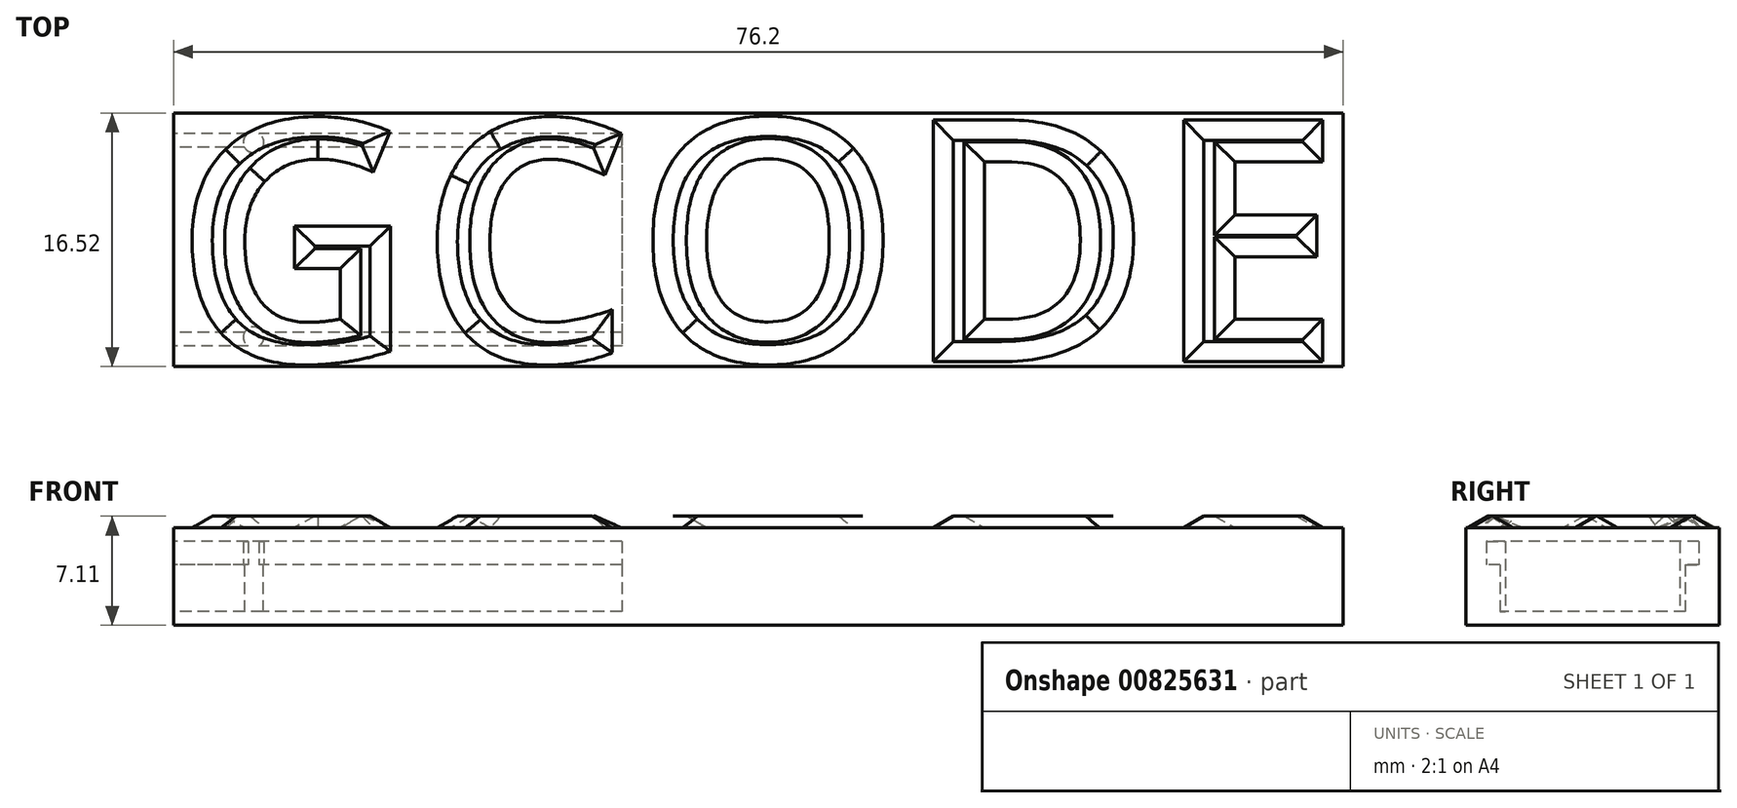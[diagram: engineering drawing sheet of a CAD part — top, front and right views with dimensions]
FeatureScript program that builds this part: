
annotation { "Feature Type Name" : "Feature", "Feature Type Description" : "" }
export const myFeature = defineFeature(function(context is Context, id is Id, definition is map)
    precondition{}
    {
        {
            var Q0;
            Q0=qCreatedBy(makeId("Top.planeOp"),FACE);
            var sketch = newSketch(context, id + "F0", { "sketchPlane" : qUnion([Q0])});
            skText(sketch, "E0", { "text": "GCODE", "fontName": "OpenSans-Bold.ttf"});
            const initialGuessF0  = {"E0": [-0.03818, -0.00794, 1, 0, 0.01588]};
            skSetInitialGuess(sketch, initialGuessF0);
            skSolve(sketch);
        }
        {
            var Q0;
            Q0=makeQuery(id+"F0.imprint","IMPRINT",FACE,{"disambiguationData":[TD([[makeQuery(id+"F0.imprint","IMPRINT",EDGE,{"derivedFrom":sQuery(id+"F0.wireOp",EDGE,"E0.sketch_text.stroke-0")}),-1.0]])]});
            var Q1;
            Q1=makeQuery(id+"F0.imprint","IMPRINT",FACE,{"disambiguationData":[TD([[makeQuery(id+"F0.imprint","IMPRINT",EDGE,{"derivedFrom":sQuery(id+"F0.wireOp",EDGE,"E0.sketch_text.stroke-19")}),-1.0]])]});
            var Q2;
            Q2=makeQuery(id+"F0.imprint","IMPRINT",FACE,{"disambiguationData":[TD([[makeQuery(id+"F0.imprint","IMPRINT",EDGE,{"derivedFrom":sQuery(id+"F0.wireOp",EDGE,"E0.sketch_text.stroke-48")}),-1.0]])]});
            var Q3;
            Q3=makeQuery(id+"F0.imprint","IMPRINT",FACE,{"disambiguationData":[TD([[makeQuery(id+"F0.imprint","IMPRINT",EDGE,{"derivedFrom":sQuery(id+"F0.wireOp",EDGE,"E0.sketch_text.stroke-34")}),-1.0]])]});
            var Q4;
            Q4=makeQuery(id+"F0.imprint","IMPRINT",FACE,{"disambiguationData":[TD([[makeQuery(id+"F0.imprint","IMPRINT",EDGE,{"derivedFrom":sQuery(id+"F0.wireOp",EDGE,"E0.sketch_text.stroke-60")}),-1.0]])]});
            extrude(context, id + "F1", {"entities" : qUnion([Q0, Q1, Q2, Q3, Q4]), "depth" : 0.76 * mm, "offsetDistance" : 25.4 * mm});
        }
        {
            var Q0;
            Q0=qCreatedBy(makeId("Right.planeOp"),FACE);
            var sketch = newSketch(context, id + "F2", { "sketchPlane" : qUnion([Q0])});
            skLineSegment(sketch, "E1.bottom", {"start": v(8.26, 0) * mm, "end": v(-8.26, 0) * mm});
            skLineSegment(sketch, "E1.top", {"start": v(8.26, -6.35) * mm, "end": v(-8.25, -6.35) * mm});
            skLineSegment(sketch, "E1.left", {"start": v(8.26, 0) * mm, "end": v(8.26, -6.35) * mm});
            skLineSegment(sketch, "E1.right", {"start": v(-8.26, 0) * mm, "end": v(-8.25, -6.35) * mm});
            skSolve(sketch);
        }
        {
            var Q0;
            Q0=makeQuery(id+"F2.imprint","IMPRINT",FACE,{"disambiguationData":[TD([[makeQuery(id+"F2.imprint","IMPRINT",EDGE,{"derivedFrom":sQuery(id+"F2.wireOp",EDGE,"E1.bottom")}),1.0]])]});
            extrude(context, id + "F3", {"entities" : qUnion([Q0]), "operationType" : NewBodyOperationType.ADD, "endBound" : BoundingType.SYMMETRIC, "depth" : 76.2 * mm, "offsetDistance" : 25.4 * mm});
        }
        {
            var Q0;
            Q0=makeQuery(id+"F1.opExtrude","CAP_EDGE",EDGE,{"disambiguationData":[OSD([sQuery(id+"F0.wireOp",EDGE,"E0.sketch_text.stroke-57")])],"isStart":false});
            var Q1;
            Q1=makeQuery(id+"F1.opExtrude","CAP_FACE",FACE,{"disambiguationData":[OSD([sQuery(id+"F0.wireOp",EDGE,"E0.sketch_text.stroke-48"),sQuery(id+"F0.wireOp",EDGE,"E0.sketch_text.stroke-49"),sQuery(id+"F0.wireOp",EDGE,"E0.sketch_text.stroke-50"),sQuery(id+"F0.wireOp",EDGE,"E0.sketch_text.stroke-51"),sQuery(id+"F0.wireOp",EDGE,"E0.sketch_text.stroke-52"),sQuery(id+"F0.wireOp",EDGE,"E0.sketch_text.stroke-53"),sQuery(id+"F0.wireOp",EDGE,"E0.sketch_text.stroke-54"),sQuery(id+"F0.wireOp",EDGE,"E0.sketch_text.stroke-55"),sQuery(id+"F0.wireOp",EDGE,"E0.sketch_text.stroke-56"),sQuery(id+"F0.wireOp",EDGE,"E0.sketch_text.stroke-57"),sQuery(id+"F0.wireOp",EDGE,"E0.sketch_text.stroke-58"),sQuery(id+"F0.wireOp",EDGE,"E0.sketch_text.stroke-59")])],"isStart":false});
            var Q2;
            Q2=makeQuery(id+"F1.opExtrude","CAP_FACE",FACE,{"disambiguationData":[OSD([sQuery(id+"F0.wireOp",EDGE,"E0.sketch_text.stroke-34"),sQuery(id+"F0.wireOp",EDGE,"E0.sketch_text.stroke-35"),sQuery(id+"F0.wireOp",EDGE,"E0.sketch_text.stroke-36"),sQuery(id+"F0.wireOp",EDGE,"E0.sketch_text.stroke-37"),sQuery(id+"F0.wireOp",EDGE,"E0.sketch_text.stroke-38"),sQuery(id+"F0.wireOp",EDGE,"E0.sketch_text.stroke-39"),sQuery(id+"F0.wireOp",EDGE,"E0.sketch_text.stroke-40"),sQuery(id+"F0.wireOp",EDGE,"E0.sketch_text.stroke-41"),sQuery(id+"F0.wireOp",EDGE,"E0.sketch_text.stroke-42"),sQuery(id+"F0.wireOp",EDGE,"E0.sketch_text.stroke-43"),sQuery(id+"F0.wireOp",EDGE,"E0.sketch_text.stroke-44"),sQuery(id+"F0.wireOp",EDGE,"E0.sketch_text.stroke-45"),sQuery(id+"F0.wireOp",EDGE,"E0.sketch_text.stroke-46"),sQuery(id+"F0.wireOp",EDGE,"E0.sketch_text.stroke-47")])],"isStart":false});
            var Q3;
            Q3=makeQuery(id+"F1.opExtrude","CAP_FACE",FACE,{"disambiguationData":[OSD([sQuery(id+"F0.wireOp",EDGE,"E0.sketch_text.stroke-60"),sQuery(id+"F0.wireOp",EDGE,"E0.sketch_text.stroke-61"),sQuery(id+"F0.wireOp",EDGE,"E0.sketch_text.stroke-62"),sQuery(id+"F0.wireOp",EDGE,"E0.sketch_text.stroke-63"),sQuery(id+"F0.wireOp",EDGE,"E0.sketch_text.stroke-64"),sQuery(id+"F0.wireOp",EDGE,"E0.sketch_text.stroke-65"),sQuery(id+"F0.wireOp",EDGE,"E0.sketch_text.stroke-66"),sQuery(id+"F0.wireOp",EDGE,"E0.sketch_text.stroke-67"),sQuery(id+"F0.wireOp",EDGE,"E0.sketch_text.stroke-68"),sQuery(id+"F0.wireOp",EDGE,"E0.sketch_text.stroke-69"),sQuery(id+"F0.wireOp",EDGE,"E0.sketch_text.stroke-70"),sQuery(id+"F0.wireOp",EDGE,"E0.sketch_text.stroke-71")])],"isStart":false});
            var Q4;
            Q4=makeQuery(id+"F1.opExtrude","CAP_FACE",FACE,{"disambiguationData":[OSD([sQuery(id+"F0.wireOp",EDGE,"E0.sketch_text.stroke-19"),sQuery(id+"F0.wireOp",EDGE,"E0.sketch_text.stroke-20"),sQuery(id+"F0.wireOp",EDGE,"E0.sketch_text.stroke-21"),sQuery(id+"F0.wireOp",EDGE,"E0.sketch_text.stroke-22"),sQuery(id+"F0.wireOp",EDGE,"E0.sketch_text.stroke-23"),sQuery(id+"F0.wireOp",EDGE,"E0.sketch_text.stroke-24"),sQuery(id+"F0.wireOp",EDGE,"E0.sketch_text.stroke-25"),sQuery(id+"F0.wireOp",EDGE,"E0.sketch_text.stroke-26"),sQuery(id+"F0.wireOp",EDGE,"E0.sketch_text.stroke-27"),sQuery(id+"F0.wireOp",EDGE,"E0.sketch_text.stroke-28"),sQuery(id+"F0.wireOp",EDGE,"E0.sketch_text.stroke-29"),sQuery(id+"F0.wireOp",EDGE,"E0.sketch_text.stroke-30"),sQuery(id+"F0.wireOp",EDGE,"E0.sketch_text.stroke-31"),sQuery(id+"F0.wireOp",EDGE,"E0.sketch_text.stroke-32"),sQuery(id+"F0.wireOp",EDGE,"E0.sketch_text.stroke-33")])],"isStart":false});
            var Q5;
            Q5=makeQuery(id+"F1.opExtrude","CAP_FACE",FACE,{"disambiguationData":[OSD([sQuery(id+"F0.wireOp",EDGE,"E0.sketch_text.stroke-0"),sQuery(id+"F0.wireOp",EDGE,"E0.sketch_text.stroke-1"),sQuery(id+"F0.wireOp",EDGE,"E0.sketch_text.stroke-2"),sQuery(id+"F0.wireOp",EDGE,"E0.sketch_text.stroke-3"),sQuery(id+"F0.wireOp",EDGE,"E0.sketch_text.stroke-4"),sQuery(id+"F0.wireOp",EDGE,"E0.sketch_text.stroke-5"),sQuery(id+"F0.wireOp",EDGE,"E0.sketch_text.stroke-6"),sQuery(id+"F0.wireOp",EDGE,"E0.sketch_text.stroke-7"),sQuery(id+"F0.wireOp",EDGE,"E0.sketch_text.stroke-8"),sQuery(id+"F0.wireOp",EDGE,"E0.sketch_text.stroke-9"),sQuery(id+"F0.wireOp",EDGE,"E0.sketch_text.stroke-10"),sQuery(id+"F0.wireOp",EDGE,"E0.sketch_text.stroke-11"),sQuery(id+"F0.wireOp",EDGE,"E0.sketch_text.stroke-12"),sQuery(id+"F0.wireOp",EDGE,"E0.sketch_text.stroke-13"),sQuery(id+"F0.wireOp",EDGE,"E0.sketch_text.stroke-14"),sQuery(id+"F0.wireOp",EDGE,"E0.sketch_text.stroke-15"),sQuery(id+"F0.wireOp",EDGE,"E0.sketch_text.stroke-16"),sQuery(id+"F0.wireOp",EDGE,"E0.sketch_text.stroke-17"),sQuery(id+"F0.wireOp",EDGE,"E0.sketch_text.stroke-18")])],"isStart":false});
            chamfer(context, id + "F4", {"entities" : qUnion([Q0, Q1, Q2, Q3, Q4, Q5]), "chamferType" : ChamferType.OFFSET_ANGLE, "width" : 0.76 * mm, "oppositeDirection" : false, "angle" : 60 * degree, "tangentPropagation" : true});
        }
        {
            var Q0;
            Q0=makeQuery(id+"F3.opExtrude","CAP_FACE",FACE,{"disambiguationData":[OSD([sQuery(id+"F2.wireOp",EDGE,"E1.bottom"),sQuery(id+"F2.wireOp",EDGE,"E1.top"),sQuery(id+"F2.wireOp",EDGE,"E1.left"),sQuery(id+"F2.wireOp",EDGE,"E1.right")])],"isStart":true});
            var sketch = newSketch(context, id + "F5", { "sketchPlane" : qUnion([Q0])});
            skLineSegment(sketch, "E2.bottom", {"start": v(-6.03, -0.89) * mm, "end": v(6.03, -0.89) * mm});
            skLineSegment(sketch, "E2.top", {"start": v(-6.03, -5.46) * mm, "end": v(6.03, -5.46) * mm});
            skLineSegment(sketch, "E2.left", {"start": v(-6.03, -2.41) * mm, "end": v(-6.03, -5.46) * mm});
            skLineSegment(sketch, "E2.right", {"start": v(6.03, -2.41) * mm, "end": v(6.03, -5.46) * mm});
            skLineSegment(sketch, "E3.0", {"start": v(-8.26, 0) * mm, "end": v(-8.26, -6.35) * mm});
            skLineSegment(sketch, "E4.0", {"start": v(-8.26, -6.35) * mm, "end": v(8.25, -6.35) * mm});
            skLineSegment(sketch, "E5.bottom", {"start": v(-6.03, -0.89) * mm, "end": v(-6.92, -0.89) * mm});
            skLineSegment(sketch, "E5.top", {"start": v(-6.03, -2.41) * mm, "end": v(-6.92, -2.41) * mm});
            skLineSegment(sketch, "E5.right", {"start": v(-6.92, -0.89) * mm, "end": v(-6.92, -2.41) * mm});
            skPoint(sketch, "E6.oppositeSnap0", {"position": v(-6.48, -2.41) * mm});
            skLineSegment(sketch, "E6.bottom", {"start": v(6.03, -0.89) * mm, "end": v(6.92, -0.89) * mm});
            skLineSegment(sketch, "E6.top", {"start": v(6.03, -2.41) * mm, "end": v(6.92, -2.41) * mm});
            skLineSegment(sketch, "E6.right", {"start": v(6.92, -0.89) * mm, "end": v(6.92, -2.41) * mm});
            skSolve(sketch);
        }
        {
            var Q0;
            Q0=makeQuery(id+"F5.imprint","IMPRINT",FACE,{"disambiguationData":[TD([[makeQuery(id+"F5.imprint","IMPRINT",EDGE,{"derivedFrom":sQuery(id+"F5.wireOp",EDGE,"E2.bottom")}),-1.0]])]});
            extrude(context, id + "F6", {"entities" : qUnion([Q0]), "operationType" : NewBodyOperationType.REMOVE, "oppositeDirection" : true, "depth" : 29.2 * mm, "offsetDistance" : 25.4 * mm});
        }
        {
            var Q0;
            Q0=makeQuery(id+"F3.opExtrude","SWEPT_FACE",FACE,{"disambiguationData":[OSD([sQuery(id+"F2.wireOp",EDGE,"E1.top")])]});
            var sketch = newSketch(context, id + "F7", { "sketchPlane" : qUnion([Q0])});
            skCircle(sketch, "E7", {"center": v(-32.9, 6.35) * mm, "radius": 0.67 * mm});
            skCircle(sketch, "E8", {"center": v(-32.9, -6.35) * mm, "radius": 0.67 * mm});
            skLineSegment(sketch, "E9.0", {"start": v(-38.1, -8.26) * mm, "end": v(-38.1, 8.25) * mm});
            skSolve(sketch);
        }
        {
            var Q0;
            Q0 = qSketchRegion(id + "F7", true);
            var Q1;
            Q1=makeQuery(id+"F6.boolean.opBoolean","COPY",FACE,{"derivedFrom":makeQuery(id+"F6.opExtrude","SWEPT_FACE",FACE,{"disambiguationData":[OSD([sQuery(id+"F5.wireOp",EDGE,"E2.bottom"),sQuery(id+"F5.wireOp",EDGE,"E5.bottom"),sQuery(id+"F5.wireOp",EDGE,"E6.bottom")])]})});
            extrude(context, id + "F8", {"entities" : qUnion([Q0]), "operationType" : NewBodyOperationType.ADD, "endBound" : BoundingType.UP_TO_SURFACE, "oppositeDirection" : true, "depth" : 25.4 * mm, "endBoundEntityFace" : qUnion([Q1]), "offsetDistance" : 25.4 * mm});
        }
    });
